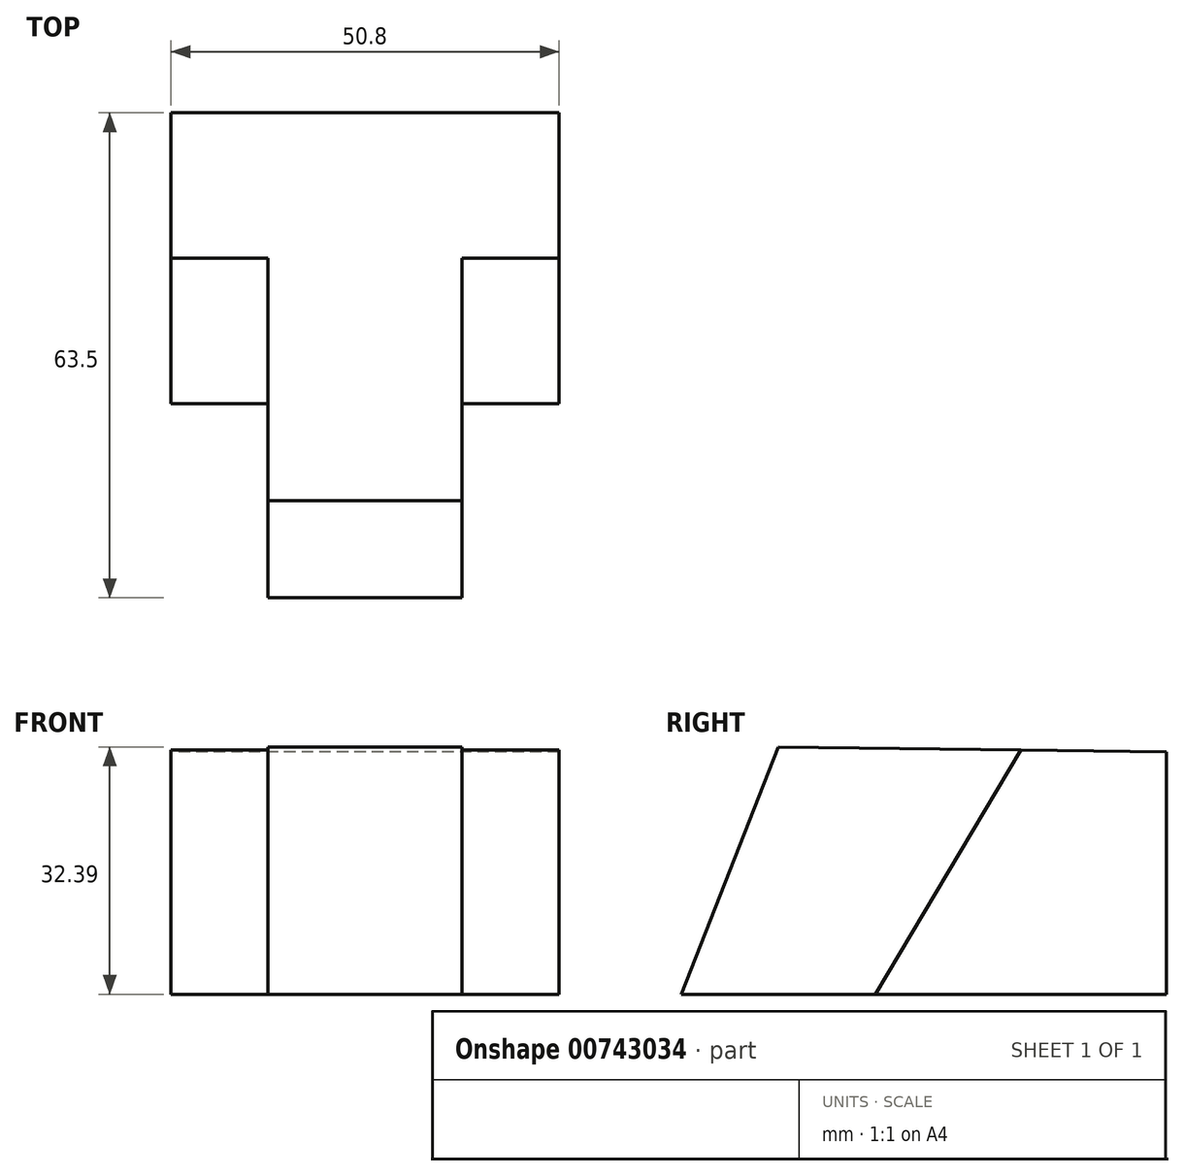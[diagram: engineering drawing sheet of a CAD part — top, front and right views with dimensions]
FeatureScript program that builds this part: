
annotation { "Feature Type Name" : "Feature", "Feature Type Description" : "" }
export const myFeature = defineFeature(function(context is Context, id is Id, definition is map)
    precondition{}
    {
        {
            var Q0;
            Q0=qCreatedBy(makeId("Right.planeOp"),FACE);
            var sketch = newSketch(context, id + "F0", { "sketchPlane" : qUnion([Q0])});
            skLineSegment(sketch, "E0", {"start": v(0, 31.75) * mm, "end": v(0, 0) * mm});
            skLineSegment(sketch, "E1", {"start": v(-63.5, 0) * mm, "end": v(-63.5, 32.55) * mm});
            skLineSegment(sketch, "E2", {"start": v(-63.5, 32.55) * mm, "end": v(0, 31.75) * mm});
            skLineSegment(sketch, "E3", {"start": v(0, 0) * mm, "end": v(-63.5, 0) * mm});
            skSolve(sketch);
        }
        {
            var Q0;
            Q0=makeQuery(id+"F0.imprint","IMPRINT",FACE,{"disambiguationData":[TD([[makeQuery(id+"F0.imprint","IMPRINT",EDGE,{"derivedFrom":sQuery(id+"F0.wireOp",EDGE,"E0")}),-1.0]])]});
            extrude(context, id + "F1", {"entities" : qUnion([Q0]), "depth" : 38.1 * mm, "offsetDistance" : 25.4 * mm});
        }
        {
            var Q0;
            Q0=makeQuery(id+"F1.opExtrude","CAP_FACE",FACE,{"disambiguationData":[OSD([sQuery(id+"F0.wireOp",EDGE,"E0"),sQuery(id+"F0.wireOp",EDGE,"E1"),sQuery(id+"F0.wireOp",EDGE,"E2"),sQuery(id+"F0.wireOp",EDGE,"E3")])],"isStart":true});
            var sketch = newSketch(context, id + "F2", { "sketchPlane" : qUnion([Q0])});
            skLineSegment(sketch, "E4", {"start": v(19.05, 31.99) * mm, "end": v(38.1, 0) * mm});
            skSolve(sketch);
        }
        {
            var Q0;
            {var subQ0=sQuery(id+"F2.wireOp",EDGE,"E4");Q0=makeQuery(id+"F2.imprint","IMPRINT",FACE,{"disambiguationData":[TD([[makeQuery(id+"F2.imprint","IMPRINT",EDGE,{"derivedFrom":subQ0}),1.0]])]});}
            extrude(context, id + "F3", {"entities" : qUnion([Q0]), "operationType" : NewBodyOperationType.REMOVE, "oppositeDirection" : true, "depth" : 12.7 * mm, "offsetDistance" : 25.4 * mm});
        }
        {
            var Q0;
            Q0=makeQuery(id+"F1.opExtrude","CAP_FACE",FACE,{"disambiguationData":[OSD([sQuery(id+"F0.wireOp",EDGE,"E0"),sQuery(id+"F0.wireOp",EDGE,"E1"),sQuery(id+"F0.wireOp",EDGE,"E2"),sQuery(id+"F0.wireOp",EDGE,"E3")])],"isStart":false});
            var sketch = newSketch(context, id + "F4", { "sketchPlane" : qUnion([Q0])});
            skLineSegment(sketch, "E5", {"start": v(-19.05, 31.99) * mm, "end": v(-38.1, 0) * mm});
            skSolve(sketch);
        }
        {
            var Q0;
            {var subQ0=sQuery(id+"F4.wireOp",EDGE,"E5");Q0=makeQuery(id+"F4.imprint","IMPRINT",FACE,{"disambiguationData":[TD([[makeQuery(id+"F4.imprint","IMPRINT",EDGE,{"derivedFrom":subQ0}),1.0]])]});}
            extrude(context, id + "F5", {"entities" : qUnion([Q0]), "operationType" : NewBodyOperationType.ADD, "depth" : 12.7 * mm, "offsetDistance" : 25.4 * mm});
        }
        {
            var Q0;
            Q0=makeQuery(id+"F3.boolean.opBoolean","COPY",FACE,{"derivedFrom":makeQuery(id+"F3.opExtrude","CAP_FACE",FACE,{"disambiguationData":[OSD([sQuery(id+"F0.wireOp",EDGE,"E1"),sQuery(id+"F0.wireOp",EDGE,"E2"),sQuery(id+"F0.wireOp",EDGE,"E3"),sQuery(id+"F2.wireOp",EDGE,"E4")])],"isStart":false})});
            var sketch = newSketch(context, id + "F6", { "sketchPlane" : qUnion([Q0])});
            skLineSegment(sketch, "E6", {"start": v(50.8, 32.39) * mm, "end": v(63.5, 0) * mm});
            skSolve(sketch);
        }
        {
            var Q0;
            {var subQ0=sQuery(id+"F6.wireOp",EDGE,"E6");Q0=makeQuery(id+"F6.imprint","IMPRINT",FACE,{"disambiguationData":[TD([[makeQuery(id+"F6.imprint","IMPRINT",EDGE,{"derivedFrom":subQ0}),1.0]])]});}
            extrude(context, id + "F7", {"entities" : qUnion([Q0]), "operationType" : NewBodyOperationType.REMOVE, "depth" : 25.4 * mm, "offsetDistance" : 25.4 * mm});
        }
        {
            var Q0;
            Q0=makeQuery(id+"F3.boolean.opBoolean","COPY",FACE,{"derivedFrom":makeQuery(id+"F3.opExtrude","CAP_FACE",FACE,{"disambiguationData":[OSD([sQuery(id+"F0.wireOp",EDGE,"E1"),sQuery(id+"F0.wireOp",EDGE,"E2"),sQuery(id+"F0.wireOp",EDGE,"E3"),sQuery(id+"F2.wireOp",EDGE,"E4")])],"isStart":false})});
            var sketch = newSketch(context, id + "F8", { "sketchPlane" : qUnion([Q0])});
            skLineSegment(sketch, "E7", {"start": v(50.8, 32.39) * mm, "end": v(63.5, 0) * mm});
            skSolve(sketch);
        }
        {
            var Q0;
            {var subQ0=sQuery(id+"F8.wireOp",EDGE,"E7");Q0=makeQuery(id+"F8.imprint","IMPRINT",FACE,{"disambiguationData":[TD([[makeQuery(id+"F8.imprint","IMPRINT",EDGE,{"derivedFrom":subQ0}),1.0]])]});}
            extrude(context, id + "F9", {"entities" : qUnion([Q0]), "operationType" : NewBodyOperationType.REMOVE, "oppositeDirection" : true, "depth" : 50.8 * mm, "offsetDistance" : 25.4 * mm});
        }
    });
